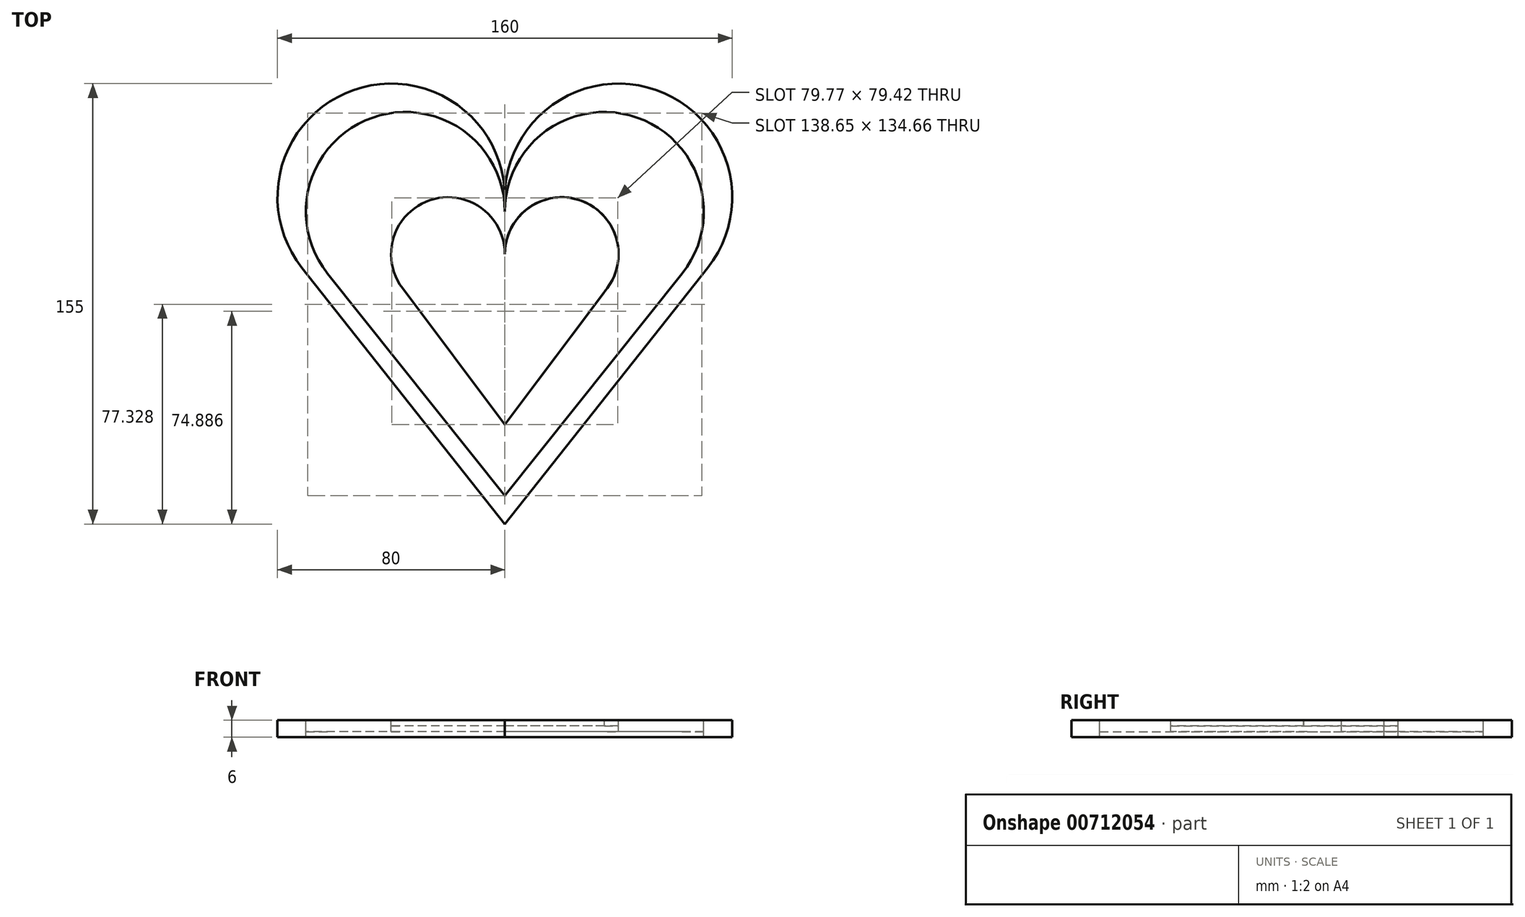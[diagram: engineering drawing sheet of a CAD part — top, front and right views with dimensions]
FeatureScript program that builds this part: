
annotation { "Feature Type Name" : "Feature", "Feature Type Description" : "" }
export const myFeature = defineFeature(function(context is Context, id is Id, definition is map)
    precondition{}
    {
        {
            var Q0;
            Q0=qCreatedBy(makeId("Top.planeOp"),FACE);
            var sketch = newSketch(context, id + "F0", { "sketchPlane" : qUnion([Q0])});
            skPoint(sketch, "E0.middle", {"position": v(0, 0) * mm});
            skArc(sketch, "E1", {"start": v(71.37, 15.18) * mm, "mid": v(53.14, 77.78) * mm, "end": v(0, 40) * mm});
            skArc(sketch, "E2", {"start": v(0, 40) * mm, "mid": v(-53.14, 77.78) * mm, "end": v(-71.37, 15.18) * mm});
            skLineSegment(sketch, "E3", {"start": v(0, -75) * mm, "end": v(-71.37, 15.18) * mm});
            skLineSegment(sketch, "E4", {"start": v(71.37, 15.18) * mm, "end": v(0, -75) * mm});
            skPoint(sketch, "E5.orphan", {"position": v(-40, -40) * mm});
            skPoint(sketch, "E0.top.end.orphan", {"position": v(40, -40) * mm});
            skPoint(sketch, "E6.start.orphan", {"position": v(0, -40) * mm});
            skPoint(sketch, "E7.5.internal.snap0", {"position": v(-20, 40) * mm});
            skPoint(sketch, "E7.5.internal.orphan", {"position": v(-20, 36.92) * mm});
            skPoint(sketch, "E8.0.internal.orphan", {"position": v(-33.3, -9.34) * mm});
            skPoint(sketch, "E9.1.internal.orphan", {"position": v(36.36, 0) * mm});
            skPoint(sketch, "E9.2.internal.orphan", {"position": v(33.85, -9.34) * mm});
            skPoint(sketch, "E9.4.internal.orphan", {"position": v(32.18, 0) * mm});
            skLineSegment(sketch, "E10.right", {"start": v(35, 6.77) * mm, "end": v(35, 6.67) * mm});
            skArc(sketch, "E11", {"start": v(0, 35) * mm, "mid": v(-46.56, 68.04) * mm, "end": v(-62.36, 13.17) * mm});
            skLineSegment(sketch, "E12", {"start": v(0, -35) * mm, "end": v(0, -65) * mm});
            skLineSegment(sketch, "E13", {"start": v(0, -65) * mm, "end": v(-62.36, 13.17) * mm});
            skLineSegment(sketch, "E14", {"start": v(62.36, 13.17) * mm, "end": v(35, -21.12) * mm});
            skLineSegment(sketch, "E15.trimOffspring", {"start": v(0, 35) * mm, "end": v(0, 40) * mm});
            skArc(sketch, "E16.trimOffspring", {"start": v(62.36, 13.17) * mm, "mid": v(46.56, 68.04) * mm, "end": v(0, 35) * mm});
            skLineSegment(sketch, "E17.trimOffspring", {"start": v(23.93, -35) * mm, "end": v(0, -65) * mm});
            skPoint(sketch, "E18.orphan", {"position": v(35, -35) * mm});
            skPoint(sketch, "E10.top.start.orphan", {"position": v(-35, -35) * mm});
            skLineSegment(sketch, "E19", {"start": v(23.93, -35) * mm, "end": v(35, -21.12) * mm});
            skArc(sketch, "E20", {"start": v(0, 20) * mm, "mid": v(-26.32, 38.97) * mm, "end": v(-36, 8) * mm});
            skArc(sketch, "E21", {"start": v(35, 6.77) * mm, "mid": v(27.07, 38.7) * mm, "end": v(0, 20) * mm});
            skLineSegment(sketch, "E22", {"start": v(0, -40) * mm, "end": v(-36, 8) * mm});
            skLineSegment(sketch, "E23", {"start": v(36, 8) * mm, "end": v(0, -40) * mm});
            skPoint(sketch, "E24.orphan", {"position": v(-20, -20) * mm});
            skPoint(sketch, "E25.orphan", {"position": v(20, -20) * mm});
            skPoint(sketch, "E26.orphan", {"position": v(0, -20) * mm});
            skSolve(sketch);
        }
        {
            var Q0;
            Q0=makeQuery(id+"F0.imprint","IMPRINT",FACE,{"disambiguationData":[TD([[makeQuery(id+"F0.imprint","IMPRINT",EDGE,{"derivedFrom":sQuery(id+"F0.wireOp",EDGE,"E1")}),1.0]])]});
            extrude(context, id + "F1", {"entities" : qUnion([Q0]), "oppositeDirection" : true, "depth" : 6 * mm, "offsetDistance" : 25 * mm});
        }
        {
            var Q0;
            Q0=makeQuery(id+"F0.imprint","IMPRINT",FACE,{"disambiguationData":[TD([[makeQuery(id+"F0.imprint","IMPRINT",EDGE,{"derivedFrom":sQuery(id+"F0.wireOp",EDGE,"E11")}),1.0]])]});
            extrude(context, id + "F2", {"entities" : qUnion([Q0]), "oppositeDirection" : true, "depth" : 4 * mm, "offsetDistance" : 25 * mm});
        }
        {
            var Q0;
            {var subQ4=sQuery(id+"F0.wireOp",EDGE,"E10.right");Q0=makeQuery(id+"F0.imprint","IMPRINT",FACE,{"disambiguationData":[TD([[makeQuery(id+"F0.imprint","IMPRINT",EDGE,{"derivedFrom":subQ4}),-1.0]])]});}
            extrude(context, id + "F3", {"entities" : qUnion([Q0]), "oppositeDirection" : true, "depth" : 2 * mm, "offsetDistance" : 25 * mm});
        }
    });
